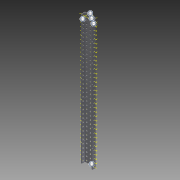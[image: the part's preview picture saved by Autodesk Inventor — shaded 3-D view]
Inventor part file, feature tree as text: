
AUTODESK INVENTOR PART (.ipt)
format: ipt  version: 2015 SP1 (Build 190203100, 203)  size: 2,271,232 bytes
history: native  units: in
note: dims shown in document units (in); Inventor stores cm internally (conversion verified against a paired STEP export)
features: other x181, pattern_linear x2, sheet_metal_op x1, extrude x1, imported_body x1, sketch x1
ambient origin geometry x8: Origin, YZ Plane, XZ Plane, XY Plane, X Axis, Y Axis, Z Axis, Center Point
bodies: Body1 (feature_tree)
feature tree (187):
  sheet_metal_op  "Fold1"
  other  "C-Channel"
  extrude  "length cut"  Depth=1.1811in
  other  "Work Point1"
  other  "Work Point2"
  other  "Work Point3"
  other  "top axis"
  other  "front axis"
  other  "back axis"
  pattern_linear  "top axes"  Count1=35  [1 undecoded]
  pattern_linear  "horiz axes"  Spacing1=0.5in  [1 undecoded]
  other  "Left Plane"
  other  "Right Plane"
  imported_body  "Base1"
  sketch  "Sketch1"  dims[d1=0.0in d2=1.1811in d4=0.5in d5=13.7795in d7=0.5in d8=13.7795in d10=0.5in d12=-17.5in d17=0.0in d18=0.0in d19=0.0in d20=0.0in d21=0.0in d22=0.0in]
  other  "Work Axis4"
  other  "Work Axis5"
  other  "Work Axis6"
  other  "Work Axis7"
  other  "Work Axis8"
  other  "Work Axis9"
  other  "Work Axis10"
  other  "Work Axis11"
  other  "Work Axis12"
  other  "Work Axis13"
  other  "Work Axis14"
  other  "Work Axis15"
  other  "Work Axis16"
  other  "Work Axis17"
  other  "Work Axis48"
  other  "Work Axis49"
  other  "Work Axis50"
  other  "Work Axis51"
  other  "Work Axis62"
  other  "Work Axis63"
  other  "Work Axis64"
  other  "Work Axis65"
  other  "Work Axis176"
  other  "Work Axis177"
  other  "Work Axis178"
  other  "Work Axis179"
  other  "Work Axis180"
  other  "Work Axis181"
  other  "Work Axis182"
  other  "Work Axis183"
  other  "Work Axis184"
  other  "Work Axis185"
  other  "Work Axis186"
  other  "Work Axis187"
  other  "Work Axis188"
  other  "Work Axis189"
  other  "Work Axis190"
  other  "Work Axis191"
  other  "Work Axis192"
  other  "Work Axis193"
  other  "Work Axis194"
  other  "Work Axis195"
  other  "Work Axis196"
  other  "Work Axis197"
  other  "Work Axis198"
  other  "Work Axis199"
  other  "Work Axis200"
  other  "Work Axis201"
  other  "Work Axis202"
  other  "Work Axis203"
  other  "Work Axis204"
  other  "Work Axis205"
  other  "Work Axis206"
  other  "Work Axis207"
  other  "Work Axis208"
  other  "Work Axis209"
  other  "Work Axis210"
  other  "Work Axis211"
  other  "Work Axis212"
  other  "Work Axis213"
  other  "Work Axis214"
  other  "Work Axis215"
  other  "Work Axis216"
  other  "Work Axis217"
  other  "Work Axis218"
  other  "Work Axis219"
  other  "Work Axis220"
  other  "Work Axis221"
  other  "Work Axis222"
  other  "Work Axis223"
  other  "Work Axis224"
  other  "Work Axis225"
  other  "Work Axis226"
  other  "Work Axis227"
  other  "Work Axis228"
  other  "Work Axis229"
  other  "Work Axis230"
  other  "Work Axis231"
  other  "Work Axis232"
  other  "Work Axis233"
  other  "Work Axis234"
  other  "Work Axis235"
  other  "Work Axis236"
  other  "Work Axis237"
  other  "Work Axis238"
  other  "Work Axis239"
  other  "Work Axis240"
  other  "Work Axis241"
  other  "Work Axis242"
  other  "Work Axis243"
  other  "Work Axis244"
  other  "Work Axis245"
  other  "Work Axis246"
  other  "Work Axis247"
  other  "Work Axis248"
  other  "Work Axis249"
  other  "Work Axis250"
  other  "Work Axis251"
  other  "Work Axis252"
  other  "Work Axis253"
  other  "Work Axis254"
  other  "Work Axis255"
  other  "Work Axis256"
  other  "Work Axis257"
  other  "Work Axis258"
  other  "Work Axis259"
  other  "Work Axis260"
  other  "Work Axis261"
  other  "Work Axis262"
  other  "Work Axis263"
  other  "Work Axis264"
  other  "Work Axis265"
  other  "Work Axis266"
  other  "Work Axis267"
  other  "Work Axis268"
  other  "Work Axis269"
  other  "Work Axis270"
  other  "Work Axis271"
  other  "Work Axis272"
  other  "Work Axis273"
  other  "Work Axis274"
  other  "Work Axis275"
  other  "Work Axis276"
  other  "Work Axis277"
  other  "Work Axis278"
  other  "Work Axis279"
  other  "Work Axis280"
  other  "Work Axis281"
  other  "Work Axis282"
  other  "Work Axis283"
  other  "Work Axis284"
  other  "Work Axis285"
  other  "Work Axis286"
  other  "Work Axis287"
  other  "Work Axis288"
  other  "Work Axis289"
  other  "Work Axis290"
  other  "Work Axis291"
  other  "Work Axis292"
  other  "Work Axis293"
  other  "Work Axis294"
  other  "Work Axis295"
  other  "Work Axis296"
  other  "Work Axis297"
  other  "Work Axis298"
  other  "Work Axis299"
  other  "Work Axis300"
  other  "Work Axis301"
  other  "Work Axis302"
  other  "Work Axis303"
  other  "Work Axis304"
  other  "Work Axis305"
  other  "Work Axis306"
  other  "Work Axis307"
  other  "Work Axis308"
  other  "Work Axis309"
  other  "Work Axis310"
  other  "Work Axis311"
  other  "Work Axis312"
  other  "Work Axis313"
  other  "Work Axis314"
  other  "Work Axis315"
  other  "Work Axis316"
  other  "Work Axis317"
  other  "Work Axis318"
  other  "Work Axis319"
  other  "Work Axis320"
  other  "Work Axis321"
  other  "Work Axis322"
  other  "Work Axis323"
  other  "Work Axis324"
  other  "Work Axis325"
note: 2 required parameter values undecoded (feature->parameter linkage not recoverable at this tier; creation-order binding heuristic only, values carry confidence <= 0.55)
